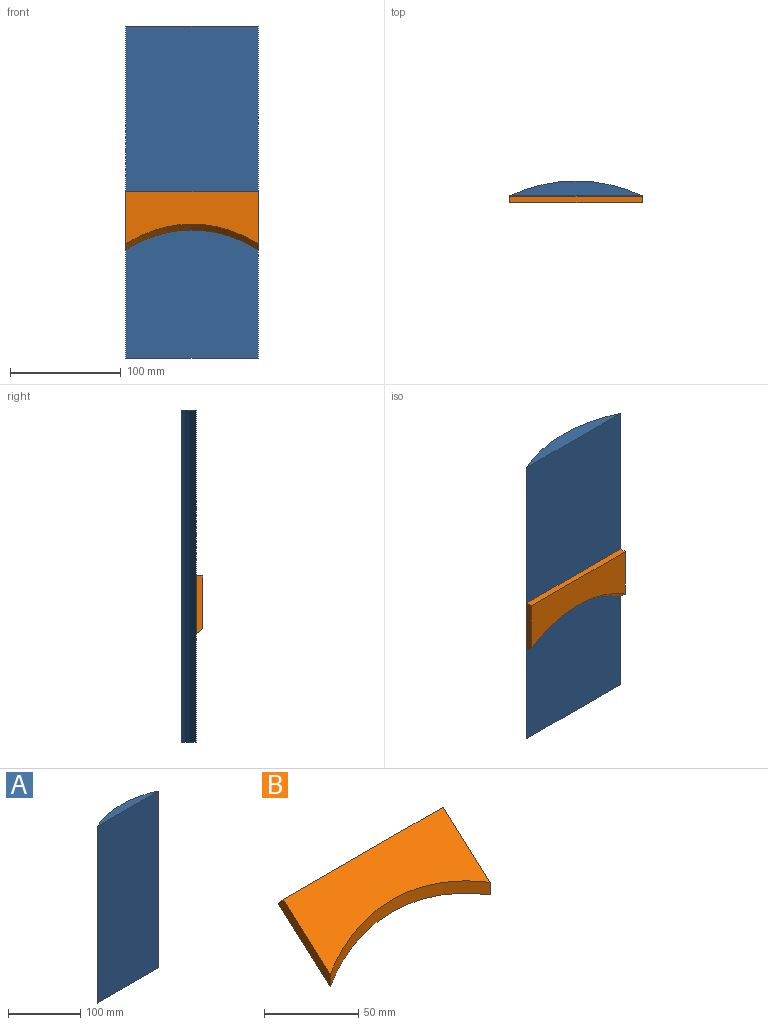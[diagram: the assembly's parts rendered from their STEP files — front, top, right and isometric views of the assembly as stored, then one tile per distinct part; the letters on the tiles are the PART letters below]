
ASSEMBLY  parts=2 mates=1
PART A: 4 faces, bbox 120x13.5x300 mm
  f0: cylinder r=140mm len=300mm, axis (0,0,-1), area 37204.5mm2, adj f1,f2,f3
  f1: plane 300x120mm, normal (0,-1,0), area 36000mm2, adj f0,f2,f3
  f2: plane 120x13.51mm, normal (0,0,1), area 1091.6mm2, adj f0,f1
  f3: plane 120x13.51mm, normal (0,0,-1), area 1091.6mm2, adj f0,f1
PART B: 6 faces, bbox 120x39.2x39.3 mm
  f0: plane 120x4.49mm, normal (0,0.75,0.66), area 720mm2, adj f1,f2,f3,f4
  f1: plane 39.28x39.16mm, normal (-1,0,0), area 298.3mm2, adj f0,f3,f4,f5
  f2: plane 39.28x39.16mm, normal (1,0,0), area 298.3mm2, adj f0,f3,f4,f5
  f3: plane 120x35.18mm, normal (0,-0.66,0.75), area 4186.5mm2, adj f0,f1,f2,f5
  f4: plane 120x39.16mm, normal (0,0.66,-0.75), area 4826.1mm2, adj f0,f1,f2,f5
  f5: cylinder r=140mm len=120mm, axis (0,0,-1), area 995.3mm2, adj f1,f2,f3,f4
PLACE A t=(448.84,-365.75,31.1)mm
PLACE B rot(axis=(1,0,0),48.4deg) t=(448.84,-270.1,-163.09)mm
MATE planar B.f4 <-> A.f1  axis (0,1,0) through (448.84,-239.26,31.1)mm
